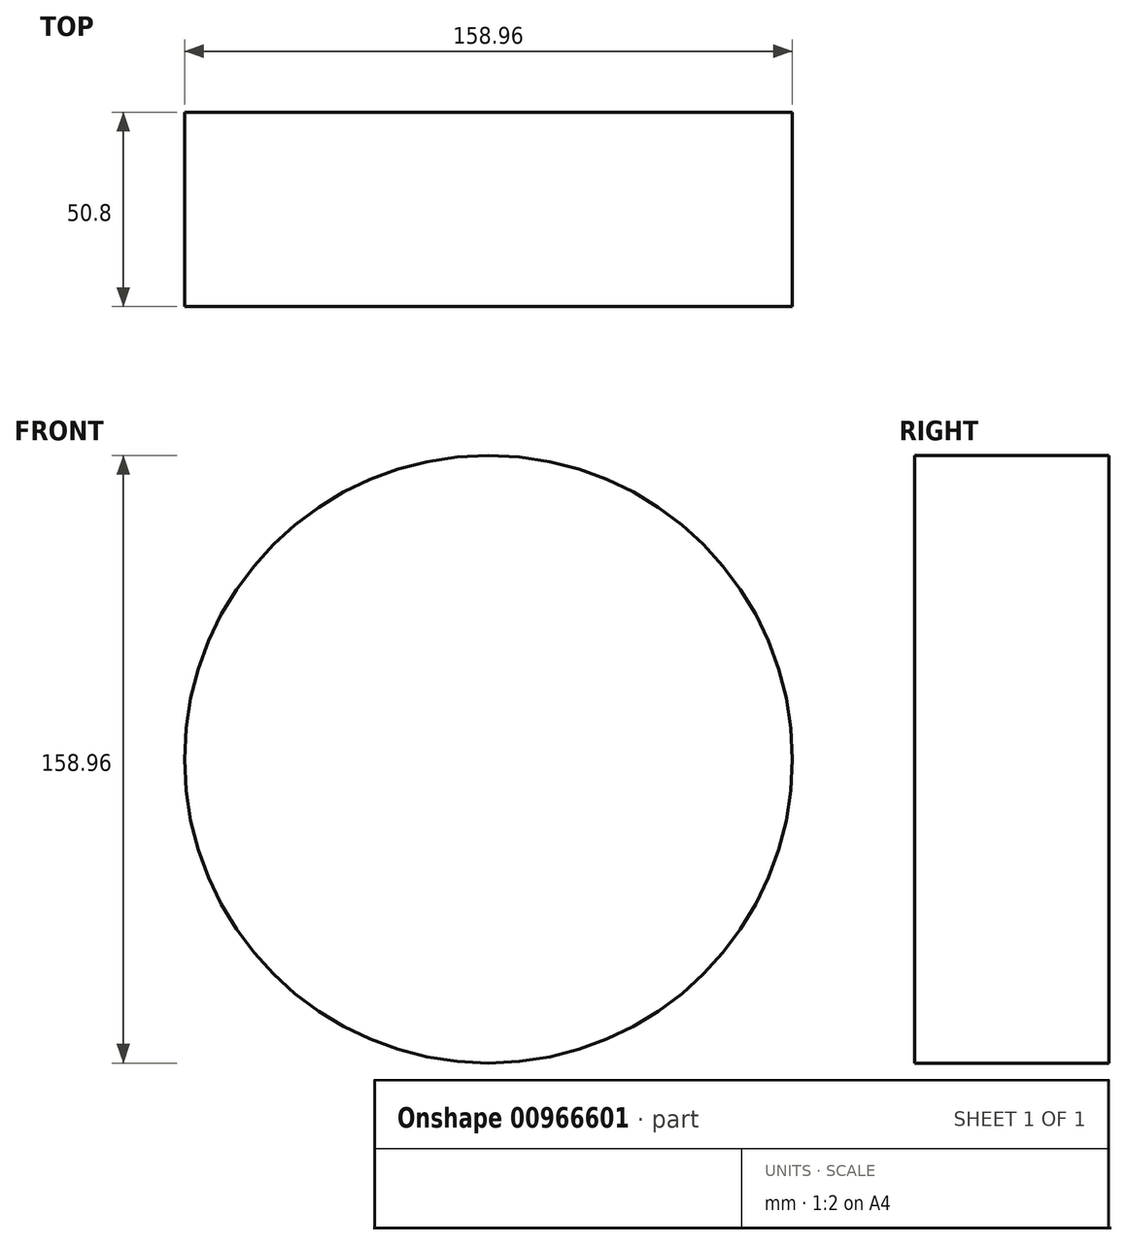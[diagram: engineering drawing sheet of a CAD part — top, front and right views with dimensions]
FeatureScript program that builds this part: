
annotation { "Feature Type Name" : "Feature", "Feature Type Description" : "" }
export const myFeature = defineFeature(function(context is Context, id is Id, definition is map)
    precondition{}
    {
        {
            var Q0;
            Q0=qCreatedBy(makeId("Front.planeOp"),FACE);
            var sketch = newSketch(context, id + "F0", { "sketchPlane" : qUnion([Q0])});
            skCircle(sketch, "E0", {"center": v(0, 0) * mm, "radius": 79.48 * mm});
            skSolve(sketch);
        }
        {
            var Q0;
            Q0=makeQuery(id+"F0.imprint","IMPRINT",FACE,{"disambiguationData":[TD([[makeQuery(id+"F0.imprint","IMPRINT",EDGE,{"derivedFrom":sQuery(id+"F0.wireOp",EDGE,"E0")}),1.0]])]});
            extrude(context, id + "F1", {"entities" : qUnion([Q0]), "depth" : 50.8 * mm, "offsetDistance" : 25.4 * mm});
        }
    });
